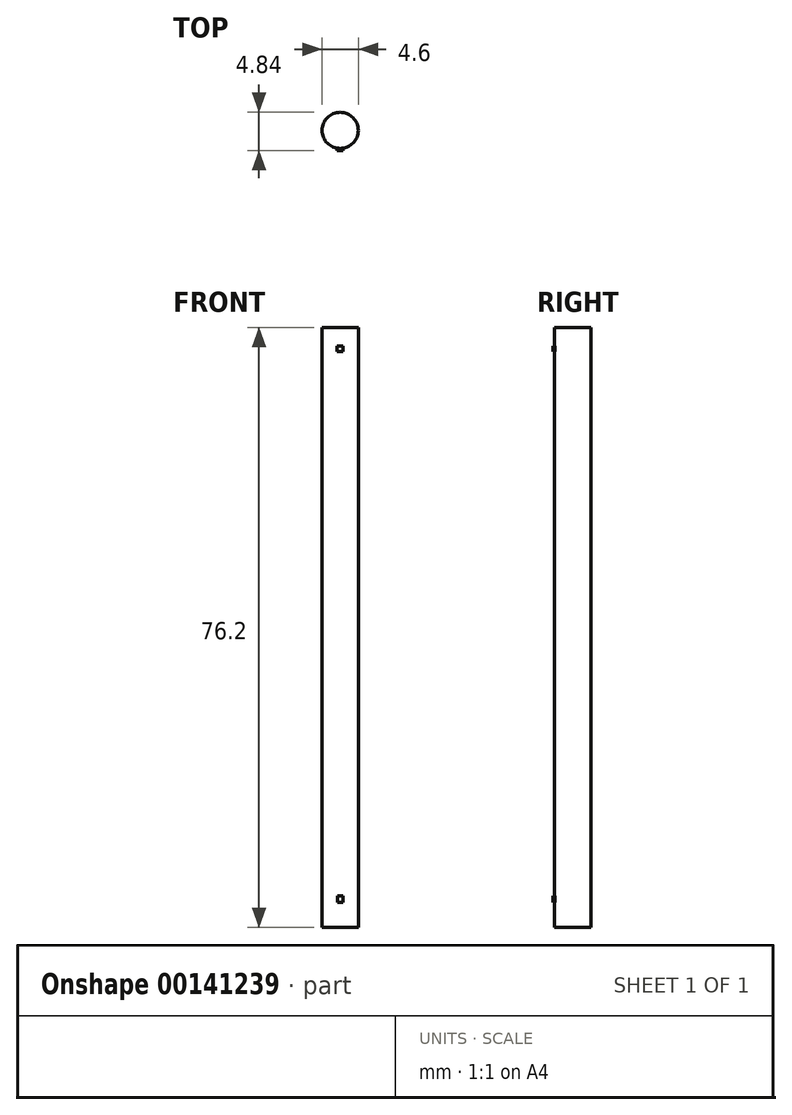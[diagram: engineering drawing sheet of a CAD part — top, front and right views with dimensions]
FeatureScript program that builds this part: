
annotation { "Feature Type Name" : "Feature", "Feature Type Description" : "" }
export const myFeature = defineFeature(function(context is Context, id is Id, definition is map)
    precondition{}
    {
        {
            var Q0;
            Q0=qCreatedBy(makeId("Top.planeOp"),FACE);
            var sketch = newSketch(context, id + "F0", { "sketchPlane" : qUnion([Q0])});
            skCircle(sketch, "E0", {"center": v(0, 0) * mm, "radius": 2.3 * mm});
            skSolve(sketch);
        }
        {
            var Q0;
            Q0 = qSketchRegion(id + "F0", true);
            extrude(context, id + "F1", {"entities" : qUnion([Q0]), "depth" : 76.2 * mm});
        }
        {
            var Q0;
            Q0=qCreatedBy(makeId("Front.planeOp"),FACE);
            var sketch = newSketch(context, id + "F2", { "sketchPlane" : qUnion([Q0])});
            skLineSegment(sketch, "E1.bottom", {"start": v(0.38, 73.15) * mm, "end": v(-0.38, 73.15) * mm});
            skLineSegment(sketch, "E1.top", {"start": v(0.38, 73.84) * mm, "end": v(-0.38, 73.84) * mm});
            skLineSegment(sketch, "E1.left", {"start": v(0.38, 73.15) * mm, "end": v(0.38, 73.84) * mm});
            skLineSegment(sketch, "E1.right", {"start": v(-0.38, 73.15) * mm, "end": v(-0.38, 73.84) * mm});
            skPoint(sketch, "E1.middle", {"position": v(0, 73.5) * mm});
            skLineSegment(sketch, "E2.bottom", {"start": v(0.37, 3.15) * mm, "end": v(-0.37, 3.15) * mm});
            skLineSegment(sketch, "E2.top", {"start": v(0.37, 3.97) * mm, "end": v(-0.37, 3.97) * mm});
            skLineSegment(sketch, "E2.left", {"start": v(0.37, 3.15) * mm, "end": v(0.37, 3.97) * mm});
            skLineSegment(sketch, "E2.right", {"start": v(-0.37, 3.15) * mm, "end": v(-0.37, 3.97) * mm});
            skPoint(sketch, "E2.middle", {"position": v(0, 3.56) * mm});
            skSolve(sketch);
        }
        {
            var Q0;
            Q0 = qSketchRegion(id + "F2", true);
            extrude(context, id + "F3", {"entities" : qUnion([Q0]), "operationType" : NewBodyOperationType.ADD, "depth" : 2.54 * mm});
        }
    });
